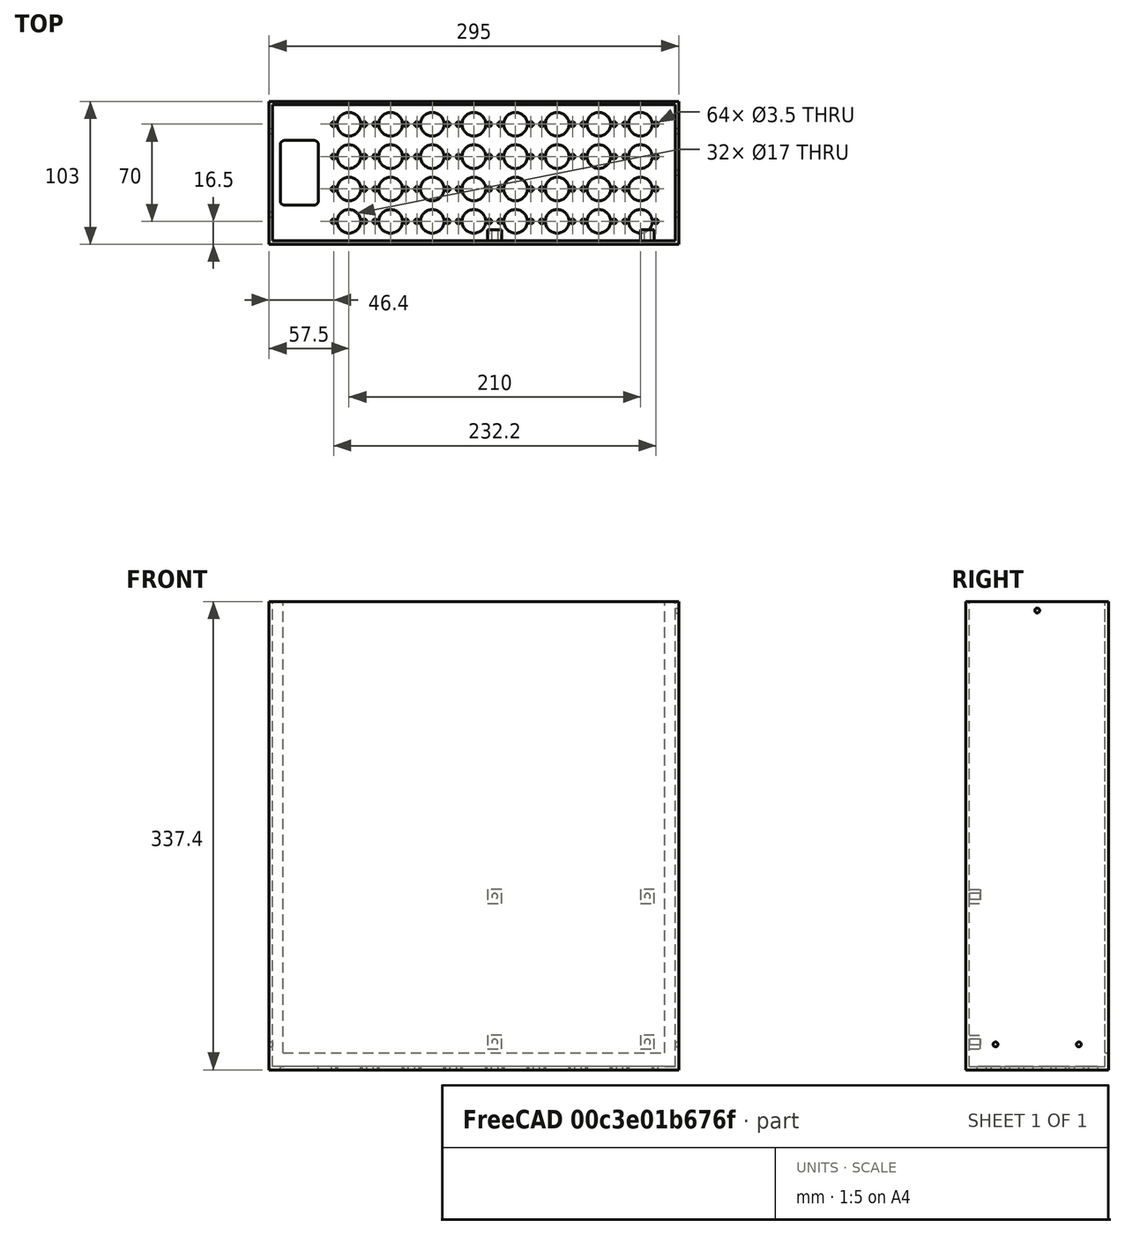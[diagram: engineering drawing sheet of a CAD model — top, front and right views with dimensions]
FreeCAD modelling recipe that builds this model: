
FCSTD DOCUMENT  (FreeCAD 0.21R33771 (Git))
Label: Main case multiplexer
License: All rights reserved
LicenseURL: http://en.wikipedia.org/wiki/All_rights_reserved
objects: Sketcher::SketchObject×8, TechDraw::DrawViewDimension×7, PartDesign::Pad×4, PartDesign::LinearPattern×4, PartDesign::Pocket×4, PartDesign::MultiTransform×2, TechDraw::DrawSVGTemplate×2, TechDraw::DrawPage×2, TechDraw::DrawViewBalloon×2, Mesh::Feature×1, PartDesign::Body×1, TechDraw::DrawProjGroupItem×1, TechDraw::DrawProjGroup×1
note: 41 computed .brp shape members not serialized (recipe doc carries the construction recipe); baked Part::Feature solids carry a one-line shape summary decoded from their .brp

FEATURE [Sketcher::SketchObject] Sketch
  FullyConstrained = true
  MapMode = 5
  Support = -> [XY_Plane]
  sketch-geometry (4):
    g0: LineSegment StartX=-147.5 StartY=51.5 StartZ=0 EndX=147.5 EndY=51.5 EndZ=0
    g1: LineSegment StartX=147.5 StartY=51.5 StartZ=0 EndX=147.5 EndY=-51.5 EndZ=0
    g2: LineSegment StartX=147.5 StartY=-51.5 StartZ=0 EndX=-147.5 EndY=-51.5 EndZ=0
    g3: LineSegment StartX=-147.5 StartY=-51.5 StartZ=0 EndX=-147.5 EndY=51.5 EndZ=0
  constraints (11):
    c: Coincident(g0,g1)
    c: Coincident(g1,g2)
    c: Coincident(g2,g3)
    c: Coincident(g3,g0)
    c: Horizontal(g0)
    c: Horizontal(g2)
    c: Vertical(g1)
    c: Vertical(g3)
    c: Symmetric(g0,g1,g-1)
    c: DistanceX(g0,g0) = 295
    c: DistanceY(g1,g1) = 103
FEATURE [PartDesign::Pad] Pad  label="Rear panel"
  Direction = (0,0,1)
  Length = 2.4
  Length2 = 10
  Profile = -> Sketch
  ReferenceAxis = -> Sketch [N_Axis]
  Type = 0
FEATURE [Sketcher::SketchObject] Sketch001
  FullyConstrained = true
  MapMode = 5
  Placement = pos=(0,0,2.4) rot=(0,0,1;0rad)
  Support = -> [Pad]
  sketch-geometry (14):
    g0: LineSegment StartX=-147.5 StartY=51.5 StartZ=0 EndX=147.5 EndY=51.5 EndZ=0
    g1: LineSegment StartX=147.5 StartY=51.5 StartZ=0 EndX=147.5 EndY=-51.5 EndZ=0
    g2: LineSegment StartX=147.5 StartY=-51.5 StartZ=0 EndX=-147.5 EndY=-51.5 EndZ=0
    g3: LineSegment StartX=-147.5 StartY=-51.5 StartZ=0 EndX=-147.5 EndY=51.5 EndZ=0
    g4: LineSegment StartX=-145 StartY=49 StartZ=0 EndX=145 EndY=49 EndZ=0
    g5: LineSegment StartX=145 StartY=49 StartZ=0 EndX=145 EndY=-49 EndZ=0
    g6: LineSegment StartX=145 StartY=-49 StartZ=0 EndX=-145 EndY=-49 EndZ=0
    g7: LineSegment StartX=-145 StartY=-49 StartZ=0 EndX=-145 EndY=49 EndZ=0
    g8: LineSegment StartX=-147.5 StartY=51.5 StartZ=0 EndX=-137.5 EndY=51.5 EndZ=0
    g9: LineSegment StartX=-137.5 StartY=51.5 StartZ=0 EndX=-137.5 EndY=49 EndZ=0
    g10: LineSegment StartX=-137.5 StartY=49 StartZ=0 EndX=-145 EndY=49 EndZ=0
    g11: LineSegment StartX=147.5 StartY=51.5 StartZ=0 EndX=137.5 EndY=51.5 EndZ=0
    g12: LineSegment StartX=137.5 StartY=51.5 StartZ=0 EndX=137.5 EndY=49 EndZ=0
    g13: LineSegment StartX=137.5 StartY=49 StartZ=0 EndX=145 EndY=49 EndZ=0
  constraints (38):
    c: Coincident(g0,g1)
    c: Coincident(g1,g2)
    c: Coincident(g2,g3)
    c: Coincident(g3,g0)
    c: Horizontal(g0)
    c: Horizontal(g2)
    c: Vertical(g1)
    c: Vertical(g3)
    c: Symmetric(g1,g0,g-1)
    c: DistanceX(g0,g0) = 295
    c: DistanceY(g3,g3) = 103
    c: Coincident(g4,g5)
    c: Coincident(g5,g6)
    c: Coincident(g6,g7)
    c: Coincident(g7,g4)
    c: Horizontal(g4)
    c: Horizontal(g6)
    c: Vertical(g5)
    c: Vertical(g7)
    c: Symmetric(g4,g5,g-1)
    c: DistanceX(g4,g4) = 290
    c: DistanceY(g7,g7) = 98
    c: Coincident(g3,g8)
    c: PointOnObject(g8,g0)
    c: Coincident(g8,g9)
    c: PointOnObject(g9,g4)
    c: Vertical(g9)
    c: Coincident(g9,g10)
    c: Coincident(g10,g7)
    c: DistanceX(g8,g8) = 10
    c: Coincident(g1,g11)
    c: PointOnObject(g11,g0)
    c: Coincident(g11,g12)
    c: PointOnObject(g12,g4)
    c: Coincident(g12,g13)
    c: Coincident(g13,g5)
    c: Vertical(g12)
    c: DistanceX(g11,g11) = 10
FEATURE [PartDesign::Pad] Pad001  label="Bottom and sides"
  BaseFeature = -> Pad
  Direction = (0,0,1)
  Length = 335
  Length2 = 10
  Profile = -> Sketch001
  ReferenceAxis = -> Sketch001 [N_Axis]
  Type = 0
FEATURE [Sketcher::SketchObject] Sketch002
  FullyConstrained = true
  MapMode = 5
  Placement = pos=(0,0,2.4) rot=(0,0,1;0rad)
  Support = -> [Pad001]
  sketch-geometry (4):
    g0: LineSegment StartX=-137.5 StartY=51.5 StartZ=0 EndX=137.5 EndY=51.5 EndZ=0
    g1: LineSegment StartX=137.5 StartY=51.5 StartZ=0 EndX=137.5 EndY=49 EndZ=0
    g2: LineSegment StartX=137.5 StartY=49 StartZ=0 EndX=-137.5 EndY=49 EndZ=0
    g3: LineSegment StartX=-137.5 StartY=49 StartZ=0 EndX=-137.5 EndY=51.5 EndZ=0
  constraints (11):
    c: Coincident(g0,g1)
    c: Coincident(g1,g2)
    c: Coincident(g2,g3)
    c: Coincident(g3,g0)
    c: Horizontal(g0)
    c: Vertical(g1)
    c: Vertical(g3)
    c: DistanceX(g0,g0) = 275
    c: DistanceY(g-1,g0) = 51.5
    c: DistanceY(g3,g3) = 2.5
    c: Symmetric(g1,g2,g-2)
FEATURE [PartDesign::Pad] Pad002  label="Rear top return"
  BaseFeature = -> Pad001
  Direction = (0,0,1)
  Length = 10
  Length2 = 10
  Profile = -> Sketch002
  ReferenceAxis = -> Sketch002 [N_Axis]
  Type = 0
FEATURE [Sketcher::SketchObject] Sketch007
  FullyConstrained = true
  MapMode = 5
  Placement = pos=(0,-49,0) rot=(0,0.707107,0.707107;3.14159rad)
  sketch-geometry (5):
    g0: LineSegment StartX=-130 StartY=25 StartZ=0 EndX=-120 EndY=25 EndZ=0
    g1: LineSegment StartX=-120 StartY=25 StartZ=0 EndX=-120 EndY=15 EndZ=0
    g2: LineSegment StartX=-120 StartY=15 StartZ=0 EndX=-130 EndY=15 EndZ=0
    g3: LineSegment StartX=-130 StartY=15 StartZ=0 EndX=-130 EndY=25 EndZ=0
    g4: Circle CenterX=-125 CenterY=20 CenterZ=0 NormalX=0 NormalY=0 NormalZ=1 AngleXU=0 Radius=2.1
  constraints (14):
    c: Coincident(g0,g1)
    c: Coincident(g1,g2)
    c: Coincident(g2,g3)
    c: Coincident(g3,g0)
    c: Horizontal(g0)
    c: Horizontal(g2)
    c: Vertical(g1)
    c: Vertical(g3)
    c: DistanceX(g0,g0) = 10
    c: Equal(g0,g3)
    c: Symmetric(g2,g0,g4)
    c: Diameter(g4) = 4.2
    c: DistanceY(g-1,g4) = 20
    c: DistanceX(g4,g-1) = 125
FEATURE [PartDesign::Pad] Pad003  label="PSU Standoff "
  BaseFeature = -> Pad002
  Direction = (0,1,-2e-16)
  Length = 8
  Length2 = 10
  Profile = -> Sketch007
  ReferenceAxis = -> Sketch007 [N_Axis]
  Type = 0
FEATURE [PartDesign::LinearPattern] LinearPattern004
  Direction = -> Sketch007 [H_Axis]
  Length = 110
  Occurrences = 2
FEATURE [PartDesign::LinearPattern] LinearPattern005
  Direction = -> Sketch007 [V_Axis]
  Length = 105
  Occurrences = 2
FEATURE [PartDesign::MultiTransform] MultiTransform002  label="PSU standoff array"
  BaseFeature = -> Pad003
  Originals = -> [Pad003]
  Transformations = -> [LinearPattern004,LinearPattern005]
FEATURE [Sketcher::SketchObject] Sketch008
  ExternalGeometry = -> [MultiTransform002]
  FullyConstrained = false
  MapMode = 5
  Placement = pos=(147.5,0,0) rot=(0.57735,0.57735,0.57735;2.0944rad)
  Support = -> [MultiTransform002]
  sketch-geometry (2):
    g0: Circle CenterX=-30 CenterY=18.3 CenterZ=0 NormalX=0 NormalY=0 NormalZ=1 AngleXU=0 Radius=1.75
    g1: Circle CenterX=30 CenterY=18.3 CenterZ=0 NormalX=0 NormalY=0 NormalZ=1 AngleXU=0 Radius=1.75
  constraints (4):
    c: Equal(g0,g1)
    c: Diameter(g0) = 3.5
    c: DistanceX(g0,g1) = 60
    c: Symmetric(g0,g1,g-2)
FEATURE [PartDesign::Pocket] Pocket004  label="Front side comp mounting hole"
  BaseFeature = -> MultiTransform002
  Direction = (-1,0,0)
  Length = 5
  Length2 = 5
  Profile = -> Sketch008
  ReferenceAxis = -> Sketch008 [N_Axis]
  Type = 1
FEATURE [Sketcher::SketchObject] Sketch009
  ExternalGeometry = -> [Pocket004]
  FullyConstrained = true
  MapMode = 5
  Placement = pos=(147.5,0,0) rot=(0.57735,0.57735,0.57735;2.0944rad)
  Support = -> [Pocket004]
  sketch-geometry (3):
    g0: Circle CenterX=-100 CenterY=331 CenterZ=0 NormalX=0 NormalY=0 NormalZ=1 AngleXU=0 Radius=1.75
    g1: Circle CenterX=0 CenterY=331 CenterZ=0 NormalX=0 NormalY=0 NormalZ=1 AngleXU=0 Radius=1.75
    g2: Circle CenterX=100 CenterY=331 CenterZ=0 NormalX=0 NormalY=0 NormalZ=1 AngleXU=0 Radius=1.75
  constraints (8):
    c: PointOnObject(g1,g-2)
    c: Symmetric(g2,g0,g1)
    c: Equal(g0,g1)
    c: Equal(g0,g2)
    c: Diameter(g0) = 3.5
    c: DistanceX(g0,g2) = 200
    c: Horizontal(g2,g0)
    c: DistanceY(g-1,g2) = 331
FEATURE [PartDesign::Pocket] Pocket005  label="Front bottom mounting holes"
  BaseFeature = -> Pocket004
  Direction = (-1,0,0)
  Length = 5
  Length2 = 5
  Profile = -> Sketch009
  ReferenceAxis = -> Sketch009 [N_Axis]
  Type = 0
FEATURE [Sketcher::SketchObject] Sketch005
  FullyConstrained = true
  MapMode = 5
  Placement = pos=(0,0,0) rot=(1,0,0;3.14159rad)
  Support = -> [Pocket005]
  sketch-geometry (4):
    g0: Circle CenterX=120 CenterY=-35 CenterZ=0 NormalX=0 NormalY=0 NormalZ=1 AngleXU=0 Radius=8.5
    g1: Circle CenterX=108.9 CenterY=-35 CenterZ=0 NormalX=0 NormalY=0 NormalZ=1 AngleXU=0 Radius=1.75
    g2: Circle CenterX=131.1 CenterY=-35 CenterZ=0 NormalX=0 NormalY=0 NormalZ=1 AngleXU=0 Radius=1.75
    g3: LineSegment StartX=108.9 StartY=-35 StartZ=0 EndX=131.1 EndY=-35 EndZ=0
  constraints (10):
    c: DistanceY(g0,g-1) = 35
    c: DistanceX(g-1,g0) = 120
    c: Diameter(g0) = 17
    c: Symmetric(g2,g1,g0)
    c: Equal(g1,g2)
    c: Diameter(g1) = 3.5
    c: Coincident(g3,g1)
    c: Coincident(g3,g2)
    c: Distance(g3) = 22.2
    c: Horizontal(g3)
FEATURE [TechDraw::DrawSVGTemplate] Template
  EditableTexts = APPROVER_NAME=APPROVER NAME; AUTHOR_NAME=AUTHOR NAME; DATE=YYYY-MM-DD; DN=DN; DOCUMENT_TYPE=Mechanical assembly drawing; OWNER_NAME=OWNER NAME; PM=PM; PN=PN; REVISION=REV A; RIGHTS=(R) DO NOT DUPLICATE THIS DRAWING TO THIRD PARTIES WITHOUT OWNER'S PERMISSION!; SCALE=M x:x; SHEET=99 of 99; SIZE=A3; TITLELINE-1=FreeCAD; TOLERANCE=+/- ?
  Height = 297
  Orientation = 1
  Template = /Applications/FreeCAD.app/Contents/Resources/share/Mod/TechDraw/Templates/A3_Landscape_ISO7200_Pep.svg
  Width = 420
FEATURE [TechDraw::DrawSVGTemplate] Template001
  EditableTexts = Designed_by_Name=Designed by Name; Drawing_number=Drawing number; FC-Date=Date; FC-SC=Scale; FC-SH=Sheet; FC-Title=Title; Subtitle=Subtitle; Weight=Weight
  Height = 210
  Orientation = 1
  Template = /Applications/FreeCAD.app/Contents/Resources/share/Mod/TechDraw/Templates/A4_LandscapeTD.svg
  Width = 297
FEATURE [TechDraw::DrawPage] Page001
  KeepUpdated = true
  NextBalloonIndex = 1
  ProjectionType = 0
  Template = -> Template001
FEATURE [Mesh::Feature] Mesh  label="Body (Meshed)"
FEATURE [PartDesign::Pocket] Pocket006
  BaseFeature = -> Pocket005
  Direction = (0,0,1)
  Length = 5
  Length2 = 5
  Profile = -> Sketch005
  ReferenceAxis = -> Sketch005 [N_Axis]
  Type = 2
FEATURE [PartDesign::LinearPattern] LinearPattern006
  Direction = -> Sketch005 [H_Axis]
  Length = 210
  Occurrences = 8
  Reversed = true
FEATURE [PartDesign::LinearPattern] LinearPattern007
  Direction = -> Y_Axis
  Length = 70
  Occurrences = 4
  Reversed = true
FEATURE [PartDesign::MultiTransform] MultiTransform003
  BaseFeature = -> Pocket006
  Originals = -> [Pocket006]
  Transformations = -> [LinearPattern006,LinearPattern007]
FEATURE [Sketcher::SketchObject] Sketch010
  FullyConstrained = true
  MapMode = 5
  Placement = pos=(0,0,0) rot=(1,0,0;3.14159rad)
  Support = -> [MultiTransform003]
  sketch-geometry (10):
    g0: ArcOfCircle CenterX=-136.5 CenterY=20.25 CenterZ=0 NormalX=0 NormalY=0 NormalZ=1 AngleXU=0 Radius=3 StartAngle=1.5708 EndAngle=3.14159
    g1: LineSegment StartX=-136.5 StartY=23.25 StartZ=0 EndX=-115 EndY=23.25 EndZ=0
    g2: ArcOfCircle CenterX=-115 CenterY=20.25 CenterZ=0 NormalX=0 NormalY=0 NormalZ=1 AngleXU=0 Radius=3 StartAngle=-2.58e-14 EndAngle=1.5708
    g3: LineSegment StartX=-112 StartY=20.25 StartZ=0 EndX=-112 EndY=-20.25 EndZ=0
    g4: ArcOfCircle CenterX=-115 CenterY=-20.25 CenterZ=0 NormalX=0 NormalY=0 NormalZ=1 AngleXU=0 Radius=3 StartAngle=4.71239 EndAngle=6.28319
    g5: LineSegment StartX=-115 StartY=-23.25 StartZ=0 EndX=-136.5 EndY=-23.25 EndZ=0
    g6: ArcOfCircle CenterX=-136.5 CenterY=-20.25 CenterZ=0 NormalX=0 NormalY=0 NormalZ=1 AngleXU=0 Radius=3 StartAngle=3.14159 EndAngle=4.71239
    g7: LineSegment StartX=-139.5 StartY=-20.25 StartZ=0 EndX=-139.5 EndY=20.25 EndZ=0
    g8: GeomPoint X=-139.5 Y=23.25 Z=0
    g9: GeomPoint X=-112 Y=-23.25 Z=0
  constraints (23):
    c: Tangent(g0,g1) = 1.5708
    c: Tangent(g1,g2) = 1.5708
    c: Tangent(g2,g3) = 1.5708
    c: Tangent(g3,g4) = 1.5708
    c: Tangent(g4,g5) = 1.5708
    c: Tangent(g5,g6) = 1.5708
    c: Tangent(g6,g7) = 1.5708
    c: Tangent(g7,g0) = 1.5708
    c: Horizontal(g1)
    c: Horizontal(g5)
    c: Vertical(g3)
    c: Vertical(g7)
    c: Equal(g0,g2)
    c: Equal(g4,g6)
    c: PointOnObject(g8,g1)
    c: PointOnObject(g8,g7)
    c: PointOnObject(g9,g3)
    c: PointOnObject(g9,g5)
    c: DistanceY(g4,g1) = 46.5
    c: DistanceX(g0,g2) = 27.5
    c: Radius(g0) = 3
    c: DistanceX(g3,g-1) = 112
    c: Symmetric(g4,g2,g-1)
FEATURE [PartDesign::Pocket] Pocket007
  BaseFeature = -> MultiTransform003
  Direction = (0,0,1)
  Length = 5
  Length2 = 5
  Profile = -> Sketch010
  ReferenceAxis = -> Sketch010 [N_Axis]
  Type = 2
FEATURE [PartDesign::Body] Body
  Group = -> [Sketch,Pad,Sketch001,Pad001,Sketch002,Pad002,Sketch005,Sketch007,Pad003,MultiTransform002,LinearPattern004,LinearPattern005,Sketch008,Pocket004,Sketch009,Pocket005,Pocket006,MultiTransform003,LinearPattern006,LinearPattern007,Sketch010,Pocket007]
  Origin = -> Origin
  Tip = -> Pocket007
FEATURE [TechDraw::DrawProjGroupItem] ProjItem  label="Front"
  CoarseView = false
  Direction = (0,0,1)
  Focus = 100
  HardHidden = false
  IsoCount = 0
  IsoHidden = false
  IsoVisible = false
  LockPosition = true
  Perspective = false
  Rotation = 0
  RotationVector = (1,0,0)
  ScaleType = 2
  ScrubCount = 0
  SeamHidden = false
  SeamVisible = true
  SmoothHidden = false
  SmoothVisible = true
  Source = -> [Body]
  Type = 0
  X = 0
  XDirection = (1,0,0)
  Y = 0
FEATURE [TechDraw::DrawProjGroup] ProjGroup
  Anchor = -> ProjItem
  AutoDistribute = true
  LockPosition = false
  ProjectionType = 0
  Rotation = 0
  ScaleType = 0
  Source = -> [Body]
  Views = -> [ProjItem]
  X = 210
  Y = 148.5
  spacingX = 15
  spacingY = 15
FEATURE [TechDraw::DrawViewDimension] Dimension
  AngleOverride = false
  Arbitrary = false
  ArbitraryTolerances = false
  EqualTolerance = true
  ExtensionAngle = 0
  FormatSpec = %.3f
  FormatSpecOverTolerance = %+.3f
  FormatSpecUnderTolerance = %+.3f
  Inverted = false
  LineAngle = 0
  LockPosition = false
  MeasureType = 1
  OverTolerance = 0
  References2D = -> [ProjItem]
  Rotation = 0
  ScaleType = 0
  TheoreticalExact = false
  Type = 1
  UnderTolerance = 0
  X = 1.18977
  Y = -73.2698
FEATURE [TechDraw::DrawViewDimension] Dimension001
  AngleOverride = false
  Arbitrary = false
  ArbitraryTolerances = false
  EqualTolerance = true
  ExtensionAngle = 0
  FormatSpec = %.3f
  FormatSpecOverTolerance = %+.3f
  FormatSpecUnderTolerance = %+.3f
  Inverted = false
  LineAngle = 0
  LockPosition = false
  MeasureType = 1
  OverTolerance = 0
  References2D = -> [ProjItem]
  Rotation = 0
  ScaleType = 0
  TheoreticalExact = false
  Type = 1
  UnderTolerance = 0
  X = 1.18977
  Y = -83.7016
FEATURE [TechDraw::DrawViewDimension] Dimension002
  AngleOverride = false
  Arbitrary = false
  ArbitraryTolerances = false
  EqualTolerance = true
  ExtensionAngle = 0
  FormatSpec = %.3f
  FormatSpecOverTolerance = %+.3f
  FormatSpecUnderTolerance = %+.3f
  Inverted = false
  LineAngle = 0
  LockPosition = false
  MeasureType = 1
  OverTolerance = 0
  References2D = -> [ProjItem]
  Rotation = 0
  ScaleType = 0
  TheoreticalExact = false
  Type = 2
  UnderTolerance = 0
  X = 174.27
  Y = 3.09489
FEATURE [TechDraw::DrawViewDimension] Dimension003
  AngleOverride = false
  Arbitrary = false
  ArbitraryTolerances = false
  EqualTolerance = true
  ExtensionAngle = 0
  FormatSpec = %.3f
  FormatSpecOverTolerance = %+.3f
  FormatSpecUnderTolerance = %+.3f
  Inverted = false
  LineAngle = 0
  LockPosition = false
  MeasureType = 1
  OverTolerance = 0
  References2D = -> [ProjItem]
  Rotation = 0
  ScaleType = 0
  TheoreticalExact = false
  Type = 2
  UnderTolerance = 0
  X = 161.26
  Y = 2.30171
FEATURE [TechDraw::DrawViewDimension] Dimension004
  AngleOverride = false
  Arbitrary = false
  ArbitraryTolerances = false
  EqualTolerance = true
  ExtensionAngle = 0
  FormatSpec = %.3f
  FormatSpecOverTolerance = %+.3f
  FormatSpecUnderTolerance = %+.3f
  Inverted = false
  LineAngle = 0
  LockPosition = false
  MeasureType = 1
  OverTolerance = 0
  References2D = -> [ProjItem]
  Rotation = 0
  ScaleType = 0
  TheoreticalExact = false
  Type = 1
  UnderTolerance = 0
  X = -109.236
  Y = 41.5373
FEATURE [TechDraw::DrawViewDimension] Dimension005
  AngleOverride = false
  Arbitrary = false
  ArbitraryTolerances = false
  EqualTolerance = true
  ExtensionAngle = 0
  FormatSpec = %.3f
  FormatSpecOverTolerance = %+.3f
  FormatSpecUnderTolerance = %+.3f
  Inverted = false
  LineAngle = 0
  LockPosition = false
  MeasureType = 1
  OverTolerance = 0
  References2D = -> [ProjItem]
  Rotation = 0
  ScaleType = 0
  TheoreticalExact = false
  Type = 2
  UnderTolerance = 0
  X = -83.6781
  Y = 3.95917
FEATURE [TechDraw::DrawViewBalloon] Balloon
  BubbleShape = 6
  EndType = 0
  EndTypeScale = 1
  KinkLength = 5
  LockPosition = false
  OriginX = -122.5
  OriginY = 0
  Rotation = 0
  ScaleType = 0
  ShapeScale = 1
  SourceView = -> ProjItem
  Text = 1|IEC
  TextWrapLen = -1
  X = -136.385
  Y = 9.62367
FEATURE [TechDraw::DrawViewBalloon] Balloon001
  BubbleShape = 6
  EndType = 0
  EndTypeScale = 1
  KinkLength = 5
  LockPosition = false
  OriginX = 72.5
  OriginY = 15
  Rotation = 0
  ScaleType = 0
  ShapeScale = 1
  SourceView = -> ProjItem
  Text = 3|6 Pin DIN
  TextWrapLen = -1
  X = 46.2929
  Y = 29.974
FEATURE [TechDraw::DrawViewDimension] Dimension006
  AngleOverride = false
  Arbitrary = false
  ArbitraryTolerances = false
  EqualTolerance = true
  ExtensionAngle = 0
  FormatSpec = %.3f
  FormatSpecOverTolerance = %+.3f
  FormatSpecUnderTolerance = %+.3f
  Inverted = false
  LineAngle = 0
  LockPosition = false
  MeasureType = 1
  OverTolerance = 0
  References2D = -> [ProjItem]
  Rotation = 0
  ScaleType = 0
  TheoreticalExact = false
  Type = 1
  UnderTolerance = 0
  X = -0.972781
  Y = 68.7539
FEATURE [TechDraw::DrawPage] Page
  KeepUpdated = true
  NextBalloonIndex = 4
  ProjectionType = 0
  Template = -> Template
  Views = -> [ProjGroup,Dimension,Dimension001,Dimension002,Dimension003,Dimension004,Dimension005,Balloon,Balloon001,Dimension006]
